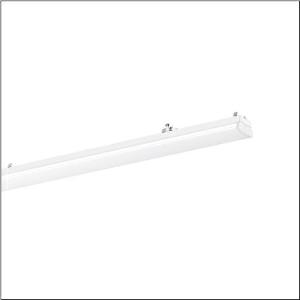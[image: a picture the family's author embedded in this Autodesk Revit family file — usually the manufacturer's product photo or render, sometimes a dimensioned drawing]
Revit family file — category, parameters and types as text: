
# Revit family: licross_r__11_recessed_opal_mo_51tl1dmn46xg_2fc5
name_source: partatom
category: Lighting Fixtures
units: mm (PartAtom-declared; Revit-internal decimal feet)

## family parameters
Cut with Voids When Loaded = No
Host = Face
Light Source = No
Part Type = Normal
Room Calculation Point = No
Round Connector Dimension = Use Diameter
Shared = No

## types (1)
- --- (1 x LED, 6320 lm, 34.3 W, 4000K)
    Apparent Load = 34 VA
    CIE Flux Codes = 44 73 91 87 100
    Color Rendering = 80
    Color Temperature = 4000K
    Default Elevation = 1800 mm
    Description = Licross® 11 recessed opal MO, luminaire insert, of sheet steel, coil coated, white, length: 1.500mm, width: 76mm, height: 87mm, LED rated luminous flux: 6.320lm, light colour: 840, control gear: ON/OFF Multilumen, with plug, 3-pole, with phase selection, mains connection: 220..240V, AC, 50/60Hz, rated input power: 34W, halogen-free wiring, primary optical cover: cover, of PMMA, light emission: direct with ceiling illumination distribution, primary light characteristic: symmetric, protection rating (complete): IP40, insulation class (complete): insulation class I (protective earthing), certification: CE, ENEC, VDE, UKCA, protection symbol: D if used in an environment without relevant dust loads with corresponding accessories, impact resistance: IK06, permissible ambient temperature for indoor applications: -35..+50°C, corresponds to IFS (International Featured Standards) requirements for safety and quality in the food industry, reducing of maximum allowable ambient temperature of 5°C with ceiling mounting, packaging unit: 1 piece
    Height = 83 mm
    Lamp = 1 x LED
    Lamp Light Flux = 6320 lm
    Lamp Power = 34.3 W
    Lamp count = 1
    Length = 1500 mm
    Luminous efficacy = 184 lm/W
    Manufacturer = Siteco
    ModVariant = No
    Model = 51TL1DMN46XG
    Mounting Place = Ceiling
    Mounting Type = Pendant
    Number of Poles = 1
    OnlyDefault = Yes
    Power Factor = 1
    Product Name = Licross® 11 recessed opal MO
    Product group = luminaire insert
    ProductGroupID = 901
    Protection Class = Protection class I
    Protection Degree = IP 40
    RLX_Detail_Level = 1
    RLX_Emergency_Light_Flux = 0 lm
    RLX_Emergency_Type = 0
    RLX_Emergency_Type_DB = No
    RlxData = <blob elided: 24781 chars, md5=59891b44>
    Socket = socket
    Standby Power = 0 W
    System Light Flux = 6320 lm
    System Power = 34 W
    Type Comments = factory setting: luminous flux: 100 % | (A | C | E) | 79 mA
    Type Image = l_1313666.jpg
    URL = http://relux.com
    VarID = @adj_031749
    Voltage = 0 V
    Weight = 0.00 kg
    Width = 76 mm

## geometry (parser evidence)
native form markers: Blend x4, Sweep x12
no freeform markers — native parametric forms only
